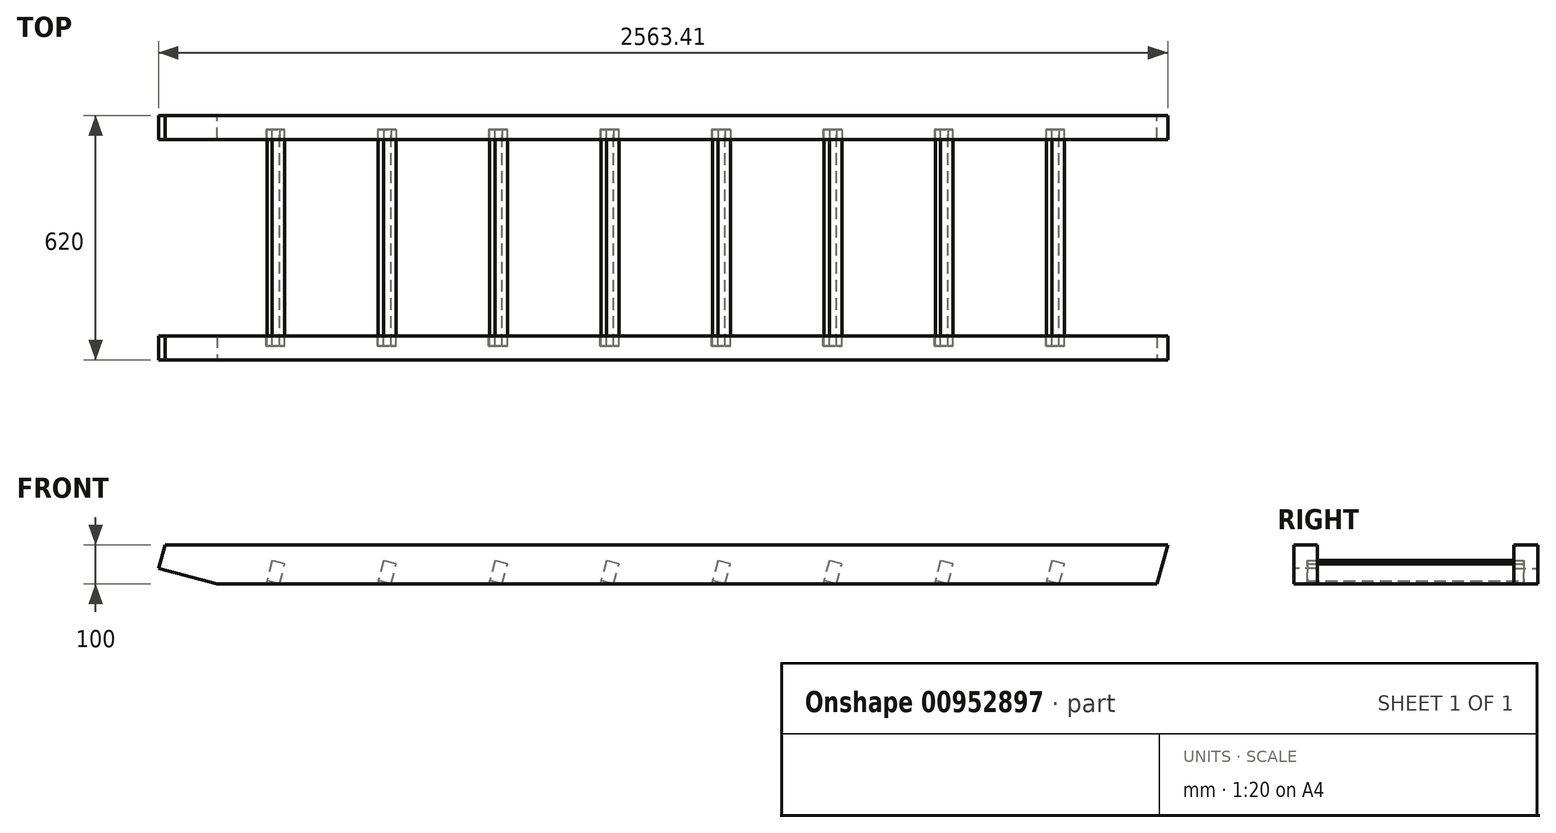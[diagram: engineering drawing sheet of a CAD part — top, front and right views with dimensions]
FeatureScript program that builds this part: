
annotation { "Feature Type Name" : "Feature", "Feature Type Description" : "" }
export const myFeature = defineFeature(function(context is Context, id is Id, definition is map)
    precondition{}
    {
        {
            var Q0;
            Q0=qCreatedBy(makeId("Front.planeOp"),FACE);
            var sketch = newSketch(context, id + "F0", { "sketchPlane" : qUnion([Q0])});
            skLineSegment(sketch, "E0", {"start": v(-501.48, 0) * mm, "end": v(1886.52, 0) * mm});
            skLineSegment(sketch, "E1", {"start": v(1886.52, 0) * mm, "end": v(1913.31, 100) * mm});
            skLineSegment(sketch, "E2", {"start": v(1913.31, 100) * mm, "end": v(-633.98, 100) * mm});
            skLineSegment(sketch, "E3", {"start": v(-633.98, 100) * mm, "end": v(-650.1, 39.82) * mm});
            skLineSegment(sketch, "E4", {"start": v(-650.1, 39.82) * mm, "end": v(-501.48, 0) * mm});
            skLineSegment(sketch, "E5", {"start": v(1913.31, 100) * mm, "end": v(1659.31, 100) * mm, "construction": true});
            skSolve(sketch);
        }
        {
            var Q0;
            Q0=makeQuery(id+"F0.imprint","IMPRINT",FACE,{"disambiguationData":[TD([[makeQuery(id+"F0.imprint","IMPRINT",EDGE,{"derivedFrom":sQuery(id+"F0.wireOp",EDGE,"E0")}),1.0]])]});
            extrude(context, id + "F1", {"entities" : qUnion([Q0]), "depth" : 60 * mm, "offsetDistance" : 25 * mm});
        }
        {
            var Q0;
            Q0=makeQuery(id+"F1.opExtrude","CAP_FACE",FACE,{"disambiguationData":[OSD([sQuery(id+"F0.wireOp",EDGE,"E0"),sQuery(id+"F0.wireOp",EDGE,"E1"),sQuery(id+"F0.wireOp",EDGE,"E2"),sQuery(id+"F0.wireOp",EDGE,"E3"),sQuery(id+"F0.wireOp",EDGE,"E4")])],"isStart":false});
            var sketch = newSketch(context, id + "F2", { "sketchPlane" : qUnion([Q0])});
            skLineSegment(sketch, "E6", {"start": v(1886.52, 0) * mm, "end": v(1920.68, 0) * mm});
            skLineSegment(sketch, "E7", {"start": v(1920.68, 0) * mm, "end": v(1934.4, 51.2) * mm});
            skLineSegment(sketch, "E8", {"start": v(1934.4, 51.2) * mm, "end": v(1902.52, 59.74) * mm});
            skLineSegment(sketch, "E9", {"start": v(1902.52, 59.74) * mm, "end": v(1886.52, 0) * mm});
            skLineSegment(sketch, "E10", {"start": v(1920.68, 0) * mm, "end": v(1888.8, 8.54) * mm});
            skLineSegment(sketch, "E11.1.0.0", {"start": v(1651.4, 51.2) * mm, "end": v(1619.52, 59.74) * mm});
            skLineSegment(sketch, "E11.1.0.1", {"start": v(1619.52, 59.74) * mm, "end": v(1603.52, 0) * mm});
            skLineSegment(sketch, "E11.1.0.2", {"start": v(1637.68, 0) * mm, "end": v(1605.8, 8.54) * mm});
            skLineSegment(sketch, "E11.1.0.3", {"start": v(1603.52, 0) * mm, "end": v(1637.68, 0) * mm});
            skLineSegment(sketch, "E11.1.0.4", {"start": v(1637.68, 0) * mm, "end": v(1651.4, 51.2) * mm});
            skLineSegment(sketch, "E11.2.0.0", {"start": v(1368.4, 51.2) * mm, "end": v(1336.52, 59.74) * mm});
            skLineSegment(sketch, "E11.2.0.1", {"start": v(1336.52, 59.74) * mm, "end": v(1320.52, 0) * mm});
            skLineSegment(sketch, "E11.2.0.2", {"start": v(1354.68, 0) * mm, "end": v(1322.8, 8.54) * mm});
            skLineSegment(sketch, "E11.2.0.3", {"start": v(1320.52, 0) * mm, "end": v(1354.68, 0) * mm});
            skLineSegment(sketch, "E11.2.0.4", {"start": v(1354.68, 0) * mm, "end": v(1368.4, 51.2) * mm});
            skLineSegment(sketch, "E11.3.0.0", {"start": v(1085.4, 51.2) * mm, "end": v(1053.52, 59.74) * mm});
            skLineSegment(sketch, "E11.3.0.1", {"start": v(1053.52, 59.74) * mm, "end": v(1037.52, 0) * mm});
            skLineSegment(sketch, "E11.3.0.2", {"start": v(1071.68, 0) * mm, "end": v(1039.8, 8.54) * mm});
            skLineSegment(sketch, "E11.3.0.3", {"start": v(1037.52, 0) * mm, "end": v(1071.68, 0) * mm});
            skLineSegment(sketch, "E11.3.0.4", {"start": v(1071.68, 0) * mm, "end": v(1085.4, 51.2) * mm});
            skLineSegment(sketch, "E11.4.0.0", {"start": v(802.4, 51.2) * mm, "end": v(770.52, 59.74) * mm});
            skLineSegment(sketch, "E11.4.0.1", {"start": v(770.52, 59.74) * mm, "end": v(754.52, 0) * mm});
            skLineSegment(sketch, "E11.4.0.2", {"start": v(788.68, 0) * mm, "end": v(756.8, 8.54) * mm});
            skLineSegment(sketch, "E11.4.0.3", {"start": v(754.52, 0) * mm, "end": v(788.68, 0) * mm});
            skLineSegment(sketch, "E11.4.0.4", {"start": v(788.68, 0) * mm, "end": v(802.4, 51.2) * mm});
            skLineSegment(sketch, "E11.5.0.0", {"start": v(519.4, 51.2) * mm, "end": v(487.52, 59.74) * mm});
            skLineSegment(sketch, "E11.5.0.1", {"start": v(487.52, 59.74) * mm, "end": v(471.52, 0) * mm});
            skLineSegment(sketch, "E11.5.0.2", {"start": v(505.68, 0) * mm, "end": v(473.8, 8.54) * mm});
            skLineSegment(sketch, "E11.5.0.3", {"start": v(471.52, 0) * mm, "end": v(505.68, 0) * mm});
            skLineSegment(sketch, "E11.5.0.4", {"start": v(505.68, 0) * mm, "end": v(519.4, 51.2) * mm});
            skLineSegment(sketch, "E11.6.0.0", {"start": v(236.4, 51.2) * mm, "end": v(204.52, 59.74) * mm});
            skLineSegment(sketch, "E11.6.0.1", {"start": v(204.52, 59.74) * mm, "end": v(188.52, 0) * mm});
            skLineSegment(sketch, "E11.6.0.2", {"start": v(222.68, 0) * mm, "end": v(190.8, 8.54) * mm});
            skLineSegment(sketch, "E11.6.0.3", {"start": v(188.52, 0) * mm, "end": v(222.68, 0) * mm});
            skLineSegment(sketch, "E11.6.0.4", {"start": v(222.68, 0) * mm, "end": v(236.4, 51.2) * mm});
            skLineSegment(sketch, "E11.7.0.0", {"start": v(-46.6, 51.2) * mm, "end": v(-78.48, 59.74) * mm});
            skLineSegment(sketch, "E11.7.0.1", {"start": v(-78.48, 59.74) * mm, "end": v(-94.48, 0) * mm});
            skLineSegment(sketch, "E11.7.0.2", {"start": v(-60.32, 0) * mm, "end": v(-92.2, 8.54) * mm});
            skLineSegment(sketch, "E11.7.0.3", {"start": v(-94.48, 0) * mm, "end": v(-60.32, 0) * mm});
            skLineSegment(sketch, "E11.7.0.4", {"start": v(-60.32, 0) * mm, "end": v(-46.6, 51.2) * mm});
            skLineSegment(sketch, "E11.8.0.0", {"start": v(-329.6, 51.2) * mm, "end": v(-361.48, 59.74) * mm});
            skLineSegment(sketch, "E11.8.0.1", {"start": v(-361.48, 59.74) * mm, "end": v(-377.48, 0) * mm});
            skLineSegment(sketch, "E11.8.0.2", {"start": v(-343.32, 0) * mm, "end": v(-375.2, 8.54) * mm});
            skLineSegment(sketch, "E11.8.0.3", {"start": v(-377.48, 0) * mm, "end": v(-343.32, 0) * mm});
            skLineSegment(sketch, "E11.8.0.4", {"start": v(-343.32, 0) * mm, "end": v(-329.6, 51.2) * mm});
            skLineSegment(sketch, "E11.direction1", {"start": v(1902.52, 59.74) * mm, "end": v(1619.52, 59.74) * mm, "construction": true});
            skLineSegment(sketch, "E12", {"start": v(-650.1, 39.82) * mm, "end": v(-617.71, 160.7) * mm, "construction": true});
            skLineSegment(sketch, "E13", {"start": v(-361.48, 59.74) * mm, "end": v(-625.8, 130.56) * mm, "construction": true});
            skLineSegment(sketch, "E14", {"start": v(-361.48, 59.74) * mm, "end": v(-332.81, 166.7) * mm, "construction": true});
            skLineSegment(sketch, "E15", {"start": v(-78.48, 59.74) * mm, "end": v(-342.52, 130.49) * mm, "construction": true});
            skLineSegment(sketch, "E16", {"start": v(1619.52, 59.74) * mm, "end": v(1650.02, 173.56) * mm, "construction": true});
            skLineSegment(sketch, "E17", {"start": v(1902.52, 59.74) * mm, "end": v(1638.48, 130.49) * mm, "construction": true});
            skSolve(sketch);
        }
        {
            var Q0;
            Q0 = qSketchRegion(id + "F2", true);
            extrude(context, id + "F3", {"entities" : qUnion([Q0]), "operationType" : NewBodyOperationType.REMOVE, "oppositeDirection" : true, "depth" : 25 * mm, "offsetDistance" : 25 * mm});
        }
        {
            var Q0;
            {var subQ0=sQuery(id+"F2.wireOp",EDGE,"E11.1.0.0");Q0=makeQuery(id+"F2.imprint","IMPRINT",FACE,{"disambiguationData":[TD([[makeQuery(id+"F2.imprint","IMPRINT",EDGE,{"derivedFrom":subQ0}),1.0]])]});}
            var Q1;
            {var subQ0=sQuery(id+"F2.wireOp",EDGE,"E11.2.0.0");Q1=makeQuery(id+"F2.imprint","IMPRINT",FACE,{"disambiguationData":[TD([[makeQuery(id+"F2.imprint","IMPRINT",EDGE,{"derivedFrom":subQ0}),1.0]])]});}
            var Q2;
            {var subQ0=sQuery(id+"F2.wireOp",EDGE,"E11.3.0.0");Q2=makeQuery(id+"F2.imprint","IMPRINT",FACE,{"disambiguationData":[TD([[makeQuery(id+"F2.imprint","IMPRINT",EDGE,{"derivedFrom":subQ0}),1.0]])]});}
            var Q3;
            {var subQ0=sQuery(id+"F2.wireOp",EDGE,"E11.4.0.0");Q3=makeQuery(id+"F2.imprint","IMPRINT",FACE,{"disambiguationData":[TD([[makeQuery(id+"F2.imprint","IMPRINT",EDGE,{"derivedFrom":subQ0}),1.0]])]});}
            var Q4;
            {var subQ0=sQuery(id+"F2.wireOp",EDGE,"E11.5.0.0");Q4=makeQuery(id+"F2.imprint","IMPRINT",FACE,{"disambiguationData":[TD([[makeQuery(id+"F2.imprint","IMPRINT",EDGE,{"derivedFrom":subQ0}),1.0]])]});}
            var Q5;
            {var subQ0=sQuery(id+"F2.wireOp",EDGE,"E11.6.0.0");Q5=makeQuery(id+"F2.imprint","IMPRINT",FACE,{"disambiguationData":[TD([[makeQuery(id+"F2.imprint","IMPRINT",EDGE,{"derivedFrom":subQ0}),1.0]])]});}
            var Q6;
            {var subQ0=sQuery(id+"F2.wireOp",EDGE,"E11.7.0.0");Q6=makeQuery(id+"F2.imprint","IMPRINT",FACE,{"disambiguationData":[TD([[makeQuery(id+"F2.imprint","IMPRINT",EDGE,{"derivedFrom":subQ0}),1.0]])]});}
            var Q7;
            {var subQ0=sQuery(id+"F2.wireOp",EDGE,"E11.8.0.0");Q7=makeQuery(id+"F2.imprint","IMPRINT",FACE,{"disambiguationData":[TD([[makeQuery(id+"F2.imprint","IMPRINT",EDGE,{"derivedFrom":subQ0}),1.0]])]});}
            extrude(context, id + "F4", {"entities" : qUnion([Q0, Q1, Q2, Q3, Q4, Q5, Q6, Q7]), "depth" : 525 * mm, "offsetDistance" : 25 * mm, "hasSecondDirection" : true, "secondDirectionOppositeDirection" : true, "secondDirectionDepth" : 25 * mm});
        }
        {
            var Q0;
            Q0=makeQuery(id+"F1.opExtrude","SWEPT_BODY",BODY,{"disambiguationData":[OSD([sQuery(id+"F0.wireOp",EDGE,"E0"),sQuery(id+"F0.wireOp",EDGE,"E1"),sQuery(id+"F0.wireOp",EDGE,"E2"),sQuery(id+"F0.wireOp",EDGE,"E3"),sQuery(id+"F0.wireOp",EDGE,"E4")])]});
            var Q1;
            {var subQ60=sQuery(id+"F2.wireOp",EDGE,"E11.1.0.0");Q1=makeQuery(id+"F2.imprint","IMPRINT",FACE,{"disambiguationData":[TD([[makeQuery(id+"F2.imprint","IMPRINT",EDGE,{"derivedFrom":subQ60}),-1.0]])]});}
            mirror(context, id + "F5", {"entities" : qUnion([Q0]), "mirrorPlane" : qUnion([Q1])});
        }
        {
            var Q0;
            Q0=makeQuery(id+"F5.opPattern","COPY",BODY,{"derivedFrom":makeQuery(id+"F1.opExtrude","SWEPT_BODY",BODY,{"disambiguationData":[OSD([sQuery(id+"F0.wireOp",EDGE,"E0"),sQuery(id+"F0.wireOp",EDGE,"E1"),sQuery(id+"F0.wireOp",EDGE,"E2"),sQuery(id+"F0.wireOp",EDGE,"E3"),sQuery(id+"F0.wireOp",EDGE,"E4")])]}),"instanceName":"1"});
            var Q1;
            Q1=makeQuery(id+"F4.opExtrude","CAP_FACE",FACE,{"disambiguationData":[OSD([sQuery(id+"F2.wireOp",EDGE,"E11.8.0.0"),sQuery(id+"F2.wireOp",EDGE,"E11.8.0.1"),sQuery(id+"F2.wireOp",EDGE,"E11.8.0.2"),sQuery(id+"F2.wireOp",EDGE,"E11.8.0.4")])],"isStart":false});
            transform(context, id + "F6", {"entities" : qUnion([Q0]), "transformType" : TransformType.TRANSLATION_DISTANCE, "transformDirection" : qUnion([Q1]), "distance" : 500 * mm, "makeCopy" : false});
        }
    });
